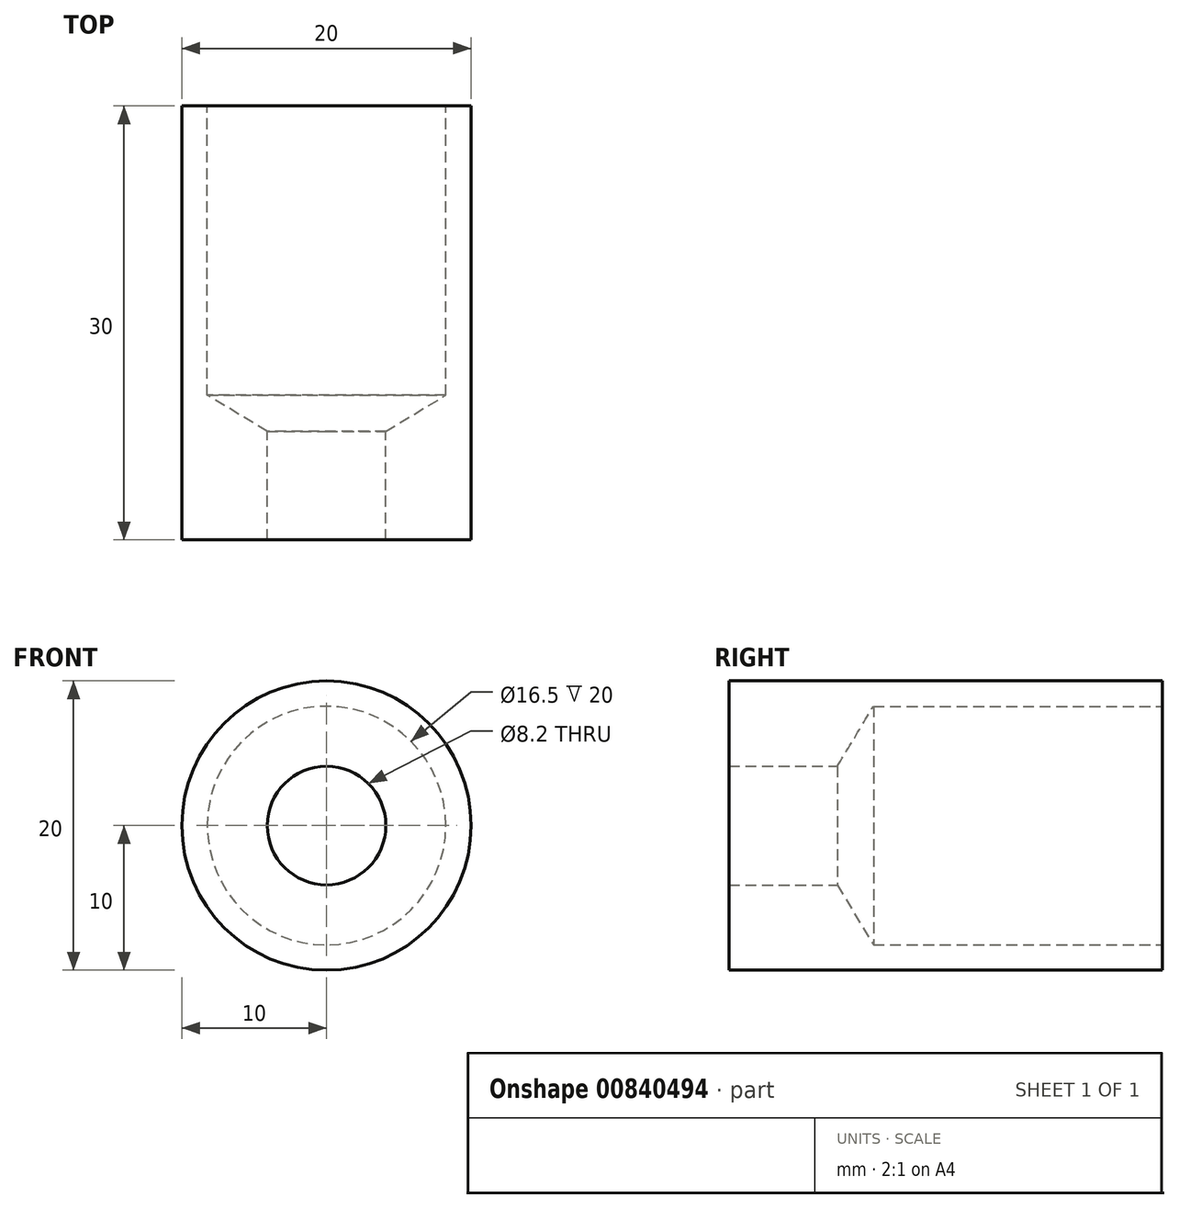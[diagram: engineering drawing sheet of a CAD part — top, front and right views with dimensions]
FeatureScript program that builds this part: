
annotation { "Feature Type Name" : "Feature", "Feature Type Description" : "" }
export const myFeature = defineFeature(function(context is Context, id is Id, definition is map)
    precondition{}
    {
        {
            var Q0;
            Q0=qCreatedBy(makeId("Front.planeOp"),FACE);
            var sketch = newSketch(context, id + "F0", { "sketchPlane" : qUnion([Q0])});
            skCircle(sketch, "E0", {"center": v(0, 0) * mm, "radius": 10 * mm});
            skSolve(sketch);
        }
        {
            var Q0;
            Q0=qSketchRegion(id+"F0",true);
            extrude(context, id + "F1", {"entities" : qUnion([Q0]), "depth" : 30 * mm, "offsetDistance" : 25 * mm});
        }
        {
            var Q0;
            Q0=qCreatedBy(makeId("Front.planeOp"),FACE);
            var sketch = newSketch(context, id + "F2", { "sketchPlane" : qUnion([Q0])});
            skPoint(sketch, "E1", {"position": v(0, 0) * mm});
            skCircle(sketch, "E2", {"center": v(0, 0) * mm, "radius": 7 * mm});
            skSolve(sketch);
        }
        {
            var Q0;
            Q0=sQuery(id+"F2.wireOp",VERTEX,"E1");
            var Q1;
            Q1=makeQuery(id+"F1.opExtrude","SWEPT_BODY",BODY,{"disambiguationData":[OSD([sQuery(id+"F0.wireOp",EDGE,"E0")])]});
            hole(context, id + "F3", {"style" : HoleStyle.SIMPLE, "endStyle" : HoleEndStyle.BLIND, "oppositeDirection" : true, "holeDiameter" : 16.5 * mm, "majorDiameter" : 5 * mm, "holeDepth" : 20 * mm, "isTappedThrough" : true, "tappedDepth" : 12 * mm, "tapClearance" : 3, "locations" : qUnion([Q0]), "scope" : qUnion([Q1])});
        }
        {
            var Q0;
            Q0=qCreatedBy(makeId("Front.planeOp"),FACE);
            var sketch = newSketch(context, id + "F4", { "sketchPlane" : qUnion([Q0])});
            skCircle(sketch, "E3", {"center": v(0, 0) * mm, "radius": 3 * mm});
            skSolve(sketch);
        }
        {
            var Q0;
            Q0=sQuery(id+"F4.wireOp",VERTEX,"E3.center");
            var Q1;
            Q1=makeQuery(id+"F1.opExtrude","SWEPT_BODY",BODY,{"disambiguationData":[OSD([sQuery(id+"F0.wireOp",EDGE,"E0")])]});
            hole(context, id + "F5", {"style" : HoleStyle.SIMPLE, "endStyle" : HoleEndStyle.BLIND, "oppositeDirection" : true, "holeDiameter" : 8.2 * mm, "majorDiameter" : 5 * mm, "holeDepth" : 100 * mm, "isTappedThrough" : true, "tappedDepth" : 12 * mm, "tapClearance" : 3, "locations" : qUnion([Q0]), "scope" : qUnion([Q1])});
        }
    });
